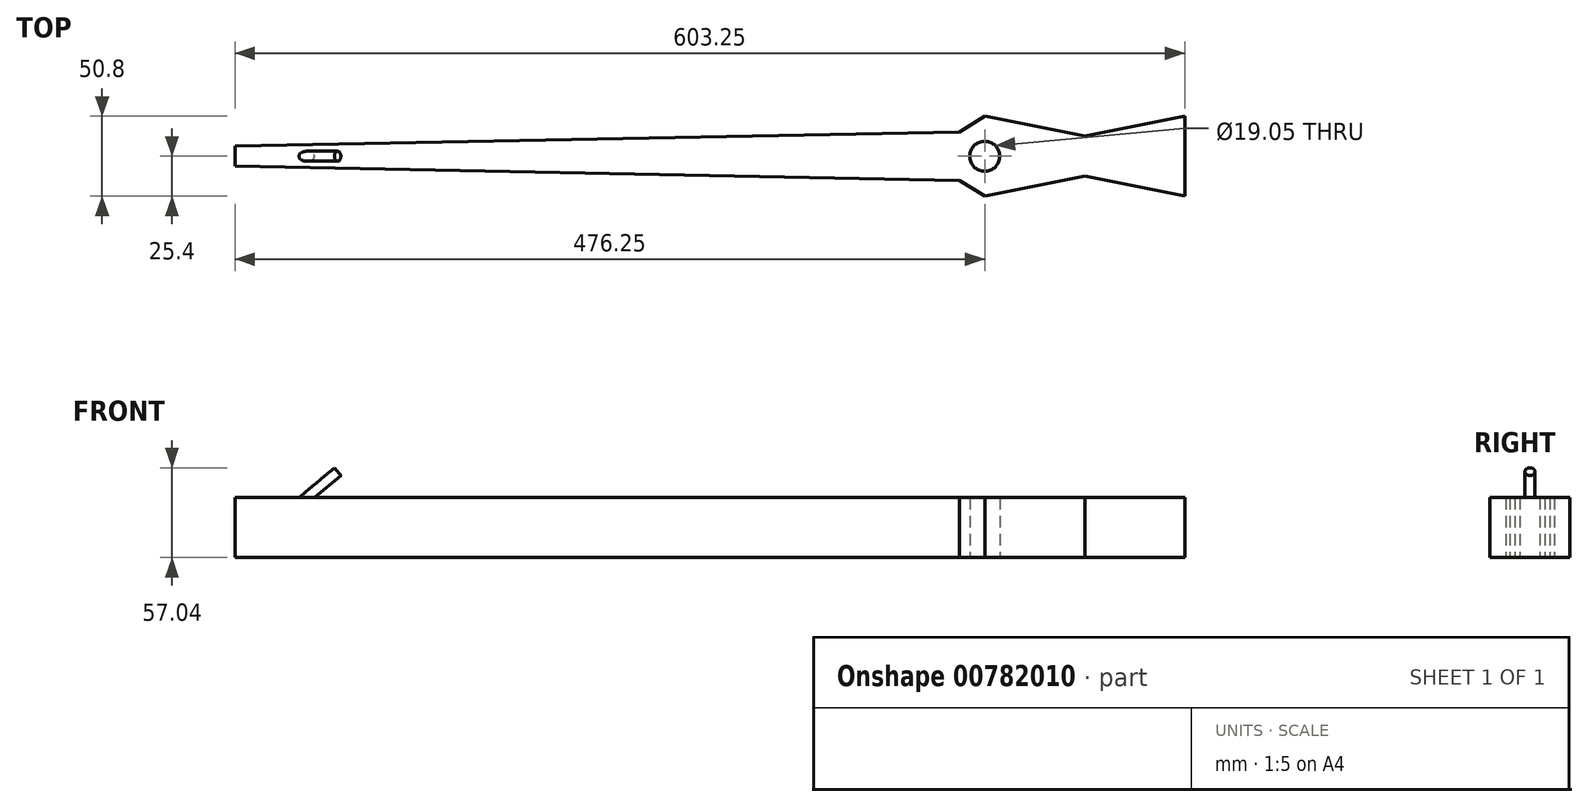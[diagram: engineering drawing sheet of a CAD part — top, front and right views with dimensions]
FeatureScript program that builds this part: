
annotation { "Feature Type Name" : "Feature", "Feature Type Description" : "" }
export const myFeature = defineFeature(function(context is Context, id is Id, definition is map)
    precondition{}
    {
        {
            var Q0;
            Q0=qCreatedBy(makeId("Top.planeOp"),FACE);
            var sketch = newSketch(context, id + "F0", { "sketchPlane" : qUnion([Q0])});
            skLineSegment(sketch, "E0", {"start": v(0, 0) * mm, "end": v(63.5, 0) * mm});
            skLineSegment(sketch, "E1", {"start": v(63.5, 0) * mm, "end": v(63.5, 25.4) * mm});
            skLineSegment(sketch, "E2", {"start": v(63.5, 0) * mm, "end": v(63.5, -25.4) * mm});
            skLineSegment(sketch, "E3", {"start": v(0, 0) * mm, "end": v(-63.5, 0) * mm});
            skLineSegment(sketch, "E4", {"start": v(-63.5, 0) * mm, "end": v(-539.75, 0) * mm});
            skLineSegment(sketch, "E5", {"start": v(-63.5, 0) * mm, "end": v(-63.5, 25.4) * mm});
            skLineSegment(sketch, "E6", {"start": v(-63.5, 0) * mm, "end": v(-63.5, -25.4) * mm});
            skLineSegment(sketch, "E7.left", {"start": v(-63.5, 25.4) * mm, "end": v(-63.5, -25.4) * mm});
            skLineSegment(sketch, "E7.right", {"start": v(63.5, 25.4) * mm, "end": v(63.5, -25.4) * mm});
            skLineSegment(sketch, "E8", {"start": v(0, 0) * mm, "end": v(0, 25.4) * mm});
            skLineSegment(sketch, "E9", {"start": v(-63.5, 25.4) * mm, "end": v(0, 12.7) * mm});
            skLineSegment(sketch, "E10", {"start": v(0, 0) * mm, "end": v(0, -25.4) * mm});
            skLineSegment(sketch, "E11", {"start": v(-63.5, -25.4) * mm, "end": v(0, -12.7) * mm});
            skLineSegment(sketch, "E12", {"start": v(0, -12.7) * mm, "end": v(63.5, -25.4) * mm});
            skLineSegment(sketch, "E13", {"start": v(0, 12.7) * mm, "end": v(63.5, 25.4) * mm});
            skPoint(sketch, "E14", {"position": v(-31.75, 0) * mm});
            skLineSegment(sketch, "E15", {"start": v(-63.5, -25.4) * mm, "end": v(-79.67, -15.33) * mm});
            skLineSegment(sketch, "E16", {"start": v(-79.67, 15.33) * mm, "end": v(-63.5, 25.4) * mm});
            skLineSegment(sketch, "E17", {"start": v(-79.67, -15.33) * mm, "end": v(-79.67, 15.33) * mm});
            skLineSegment(sketch, "E18", {"start": v(-539.75, 0) * mm, "end": v(-539.75, 6.35) * mm});
            skLineSegment(sketch, "E19", {"start": v(-539.75, 0) * mm, "end": v(-539.75, -6.35) * mm});
            skLineSegment(sketch, "E20", {"start": v(-79.67, -15.33) * mm, "end": v(-539.75, -6.35) * mm});
            skLineSegment(sketch, "E21", {"start": v(-79.67, 15.33) * mm, "end": v(-539.75, 6.35) * mm});
            skCircle(sketch, "E22", {"center": v(-63.5, 0) * mm, "radius": 9.53 * mm});
            skLineSegment(sketch, "E23", {"start": v(0, 12.7) * mm, "end": v(0, 25.4) * mm});
            skLineSegment(sketch, "E24", {"start": v(-79.67, 15.33) * mm, "end": v(-63.5, 15.33) * mm});
            skLineSegment(sketch, "E25", {"start": v(-63.5, 15.33) * mm, "end": v(-63.5, 25.4) * mm});
            skSolve(sketch);
        }
        {
            var Q0;
            Q0 = qSketchRegion(id + "F0", true);
            extrude(context, id + "F1", {"entities" : qUnion([Q0]), "depth" : 38.1 * mm, "offsetDistance" : 25.4 * mm});
        }
        {
            var Q0;
            Q0=qCreatedBy(makeId("Front.planeOp"),FACE);
            var sketch = newSketch(context, id + "F2", { "sketchPlane" : qUnion([Q0])});
            skLineSegment(sketch, "E26", {"start": v(0, 0) * mm, "end": v(-539.56, 0) * mm});
            skLineSegment(sketch, "E27", {"start": v(-539.56, 0) * mm, "end": v(-461.41, 0) * mm});
            skLineSegment(sketch, "E28", {"start": v(-461.41, 0) * mm, "end": v(-539.56, 0) * mm});
            skLineSegment(sketch, "E29", {"start": v(-539.56, 0) * mm, "end": v(-474.47, 54.6) * mm});
            skLineSegment(sketch, "E30", {"start": v(-474.47, 54.6) * mm, "end": v(-474.47, 0) * mm});
            skLineSegment(sketch, "E31", {"start": v(-539.56, 0) * mm, "end": v(-539.56, 44.45) * mm});
            skLineSegment(sketch, "E32", {"start": v(-539.56, 0) * mm, "end": v(-539.56, 38.1) * mm});
            skLineSegment(sketch, "E33", {"start": v(-539.56, 38.1) * mm, "end": v(-494.15, 38.1) * mm});
            skLineSegment(sketch, "E34", {"start": v(-474.47, 54.6) * mm, "end": v(-476.52, 57.04) * mm});
            skLineSegment(sketch, "E35", {"start": v(-494.15, 38.1) * mm, "end": v(-496.2, 40.53) * mm});
            skLineSegment(sketch, "E36", {"start": v(-496.2, 40.53) * mm, "end": v(-476.52, 57.04) * mm});
            skPoint(sketch, "E37", {"position": v(-518.27, 17.86) * mm});
            skLineSegment(sketch, "E38", {"start": v(-518.27, 17.86) * mm, "end": v(-494.15, 38.1) * mm});
            skLineSegment(sketch, "E39", {"start": v(-518.27, 17.86) * mm, "end": v(-520.3, 20.3) * mm});
            skLineSegment(sketch, "E40", {"start": v(-520.3, 20.3) * mm, "end": v(-496.2, 40.53) * mm});
            skSolve(sketch);
        }
        {
            var Q0;
            {var subQ0=sQuery(id+"F2.wireOp",EDGE,"E35");Q0=makeQuery(id+"F2.imprint","IMPRINT",FACE,{"disambiguationData":[TD([[makeQuery(id+"F2.imprint","IMPRINT",EDGE,{"derivedFrom":subQ0}),1.0]])]});}
            var Q1;
            {var subQ0=sQuery(id+"F2.wireOp",EDGE,"E34");Q1=makeQuery(id+"F2.imprint","IMPRINT",FACE,{"disambiguationData":[TD([[makeQuery(id+"F2.imprint","IMPRINT",EDGE,{"derivedFrom":subQ0}),1.0]])]});}
            var Q2;
            Q2=sQuery(id+"F2.wireOp",EDGE,"E29");
            revolve(context, id + "F3", {"operationType" : NewBodyOperationType.ADD, "surfaceOperationType" : NewSurfaceOperationType.NEW, "entities" : qUnion([Q0, Q1]), "axis" : qUnion([Q2]), "revolveType" : RevolveType.FULL});
        }
    });
